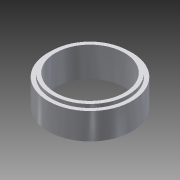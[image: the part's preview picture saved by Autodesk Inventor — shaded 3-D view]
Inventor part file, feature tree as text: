
AUTODESK INVENTOR PART (.ipt)
format: ipt  version: 2015 (Build 190159000, 159)  size: 124,416 bytes
history: native  units: in
note: dims shown in document units (in); Inventor stores cm internally (conversion verified against a paired STEP export)
features: revolve x1, sketch x1
ambient origin geometry x8: Origin, YZ Plane, XZ Plane, XY Plane, X Axis, Y Axis, Z Axis, Center Point
bodies: Solid1 (feature_tree)
feature tree (2):
  revolve  "Revolution1"  [1 undecoded]
  sketch  "Sketch1"  dims[d0=0.75in d1=1.0in d2=0.2185in d3=2.594in d4=0.5841in d5=0.5in d6=1.844in d7=0.5in d8=1.75in d9=0.25in d10=105.0deg d11=0.5in d12=0.5in d13=0.25in d14=0.375in d15=2.0in d16=0.5in d17=0.25in d18=0.234in d19=0.25in d20=2.0in d21=0.25in d22=105.0deg d23=0.125in d24=0.25in d25=2.3995in d26=0.125in d27=0.25in d28=180.0deg]
note: 1 required parameter value undecoded (feature->parameter linkage not recoverable at this tier; creation-order binding heuristic only, values carry confidence <= 0.55)
